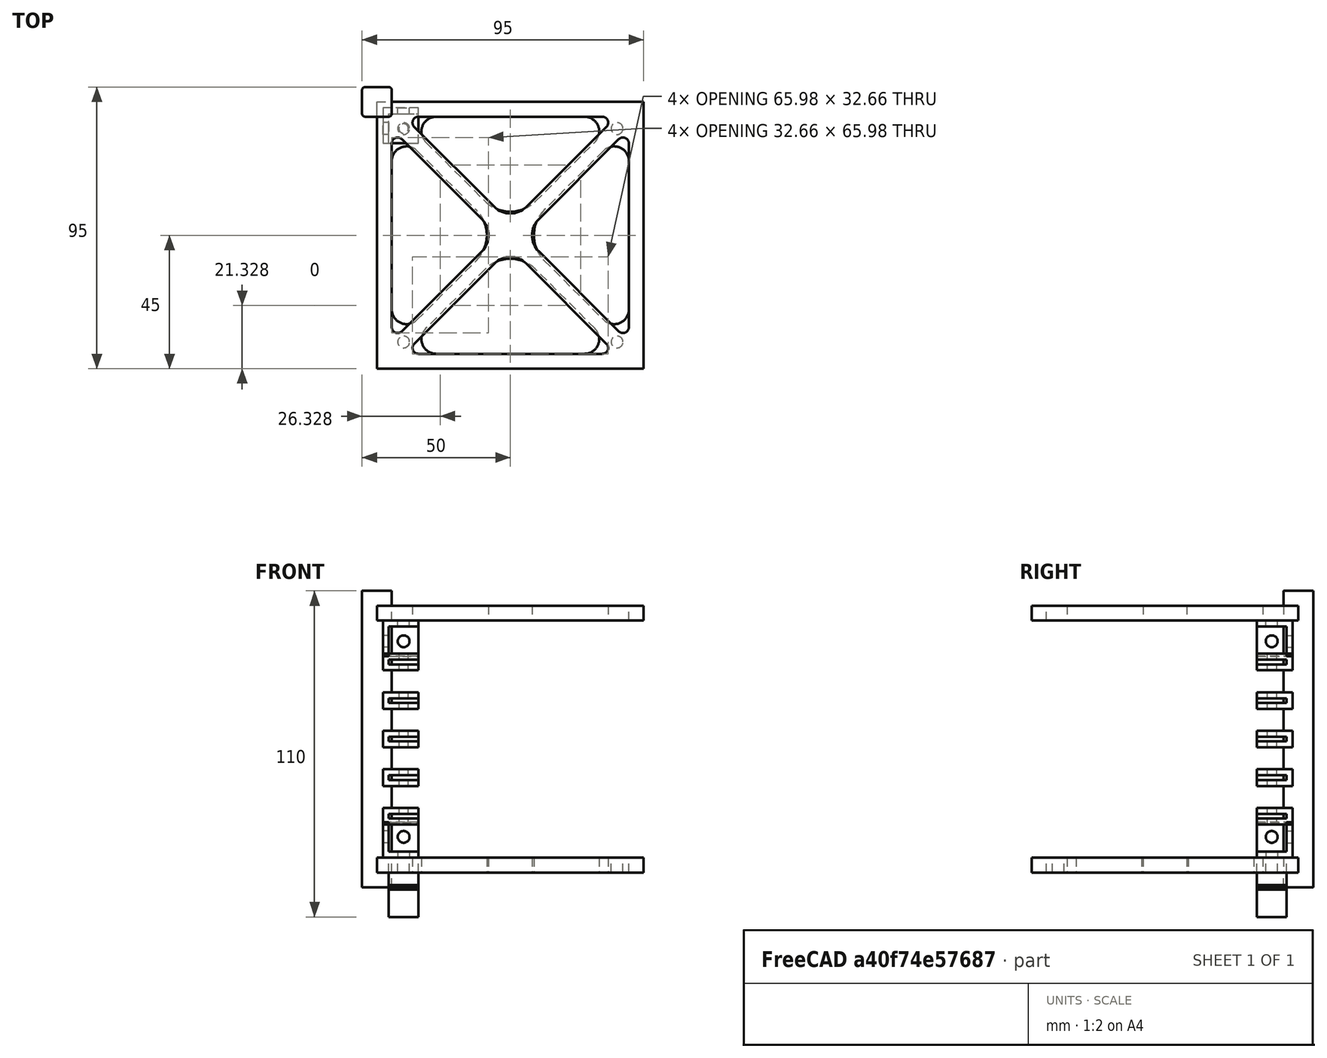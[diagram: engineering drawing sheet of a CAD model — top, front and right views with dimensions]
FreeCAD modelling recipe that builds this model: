
FCSTD DOCUMENT  (FreeCAD 0.19R24366 (Git))
Label: cube
License: Public Domain
LicenseURL: http://en.wikipedia.org/wiki/Public_domain
objects: Sketcher::SketchObject×25, PartDesign::Pad×18, PartDesign::Body×18, PartDesign::Boolean×10, PartDesign::Hole×7, App::Link×6, PartDesign::CoordinateSystem×3, App::DocumentObjectGroup×3, App::Part×3, PartDesign::Mirrored×2, PartDesign::MultiTransform×1, App::FeaturePython×1, Fem::FemSolverObjectPython×1, Fem::FemMeshShapeNetgenObject×1, Fem::ConstraintFixed×1, Fem::ConstraintForce×1, App::MaterialObjectPython×1, Fem::FemAnalysis×1
note: 109 computed .brp shape members not serialized (recipe doc carries the construction recipe); baked Part::Feature solids carry a one-line shape summary decoded from their .brp

FEATURE [Sketcher::SketchObject] Sketch
  FullyConstrained = true
  MapMode = 5
  Support = -> [XY_Plane001]
  sketch-geometry (28):
    g0: LineSegment StartX=-45 StartY=45 StartZ=0 EndX=45 EndY=45 EndZ=0
    g1: LineSegment StartX=45 StartY=45 StartZ=0 EndX=45 EndY=-45 EndZ=0
    g2: LineSegment StartX=45 StartY=-45 StartZ=0 EndX=-45 EndY=-45 EndZ=0
    g3: LineSegment StartX=-45 StartY=-45 StartZ=0 EndX=-45 EndY=45 EndZ=0
    g4: LineSegment StartX=-31 StartY=40 StartZ=0 EndX=31 EndY=40 EndZ=0
    g5: LineSegment StartX=-31 StartY=-40 StartZ=0 EndX=31 EndY=-40 EndZ=0
    g6: LineSegment StartX=-40 StartY=31 StartZ=0 EndX=-40 EndY=-31 EndZ=0
    g7: LineSegment StartX=40 StartY=31 StartZ=0 EndX=40 EndY=-31 EndZ=0
    g8: LineSegment StartX=-36.5858 StartY=32.4142 StartZ=0 EndX=-9.58579 EndY=5.41421 EndZ=0
    g9: LineSegment StartX=-32.4142 StartY=36.5858 StartZ=0 EndX=-5.41421 EndY=9.58579 EndZ=0
    g10: LineSegment StartX=5.41421 StartY=9.58579 StartZ=0 EndX=32.4142 EndY=36.5858 EndZ=0
    g11: LineSegment StartX=36.5858 StartY=32.4142 StartZ=0 EndX=9.58579 EndY=5.41421 EndZ=0
    g12: LineSegment StartX=9.58579 StartY=-5.41421 StartZ=0 EndX=36.5858 EndY=-32.4142 EndZ=0
    g13: LineSegment StartX=32.4142 StartY=-36.5858 StartZ=0 EndX=5.41421 EndY=-9.58579 EndZ=0
    g14: LineSegment StartX=-5.41421 StartY=-9.58579 StartZ=0 EndX=-32.4142 EndY=-36.5858 EndZ=0
    g15: LineSegment StartX=-36.5858 StartY=-32.4142 StartZ=0 EndX=-9.58579 EndY=-5.41421 EndZ=0
    g16: ArcOfCircle CenterX=38 CenterY=31 CenterZ=0 NormalX=0 NormalY=0 NormalZ=1 AngleXU=0 Radius=2 StartAngle=0 EndAngle=2.35619
    g17: ArcOfCircle CenterX=38 CenterY=-31 CenterZ=0 NormalX=0 NormalY=0 NormalZ=1 AngleXU=0 Radius=2 StartAngle=3.92699 EndAngle=6.28319
    g18: ArcOfCircle CenterX=31 CenterY=-38 CenterZ=0 NormalX=0 NormalY=0 NormalZ=1 AngleXU=0 Radius=2 StartAngle=4.71239 EndAngle=7.06858
    g19: ArcOfCircle CenterX=-31 CenterY=-38 CenterZ=0 NormalX=0 NormalY=0 NormalZ=1 AngleXU=0 Radius=2 StartAngle=2.35619 EndAngle=4.71239
    g20: ArcOfCircle CenterX=-38 CenterY=-31 CenterZ=0 NormalX=0 NormalY=0 NormalZ=1 AngleXU=0 Radius=2 StartAngle=3.14159 EndAngle=5.49779
    g21: ArcOfCircle CenterX=-38 CenterY=31 CenterZ=0 NormalX=0 NormalY=0 NormalZ=1 AngleXU=0 Radius=2 StartAngle=0.785398 EndAngle=3.14159
    g22: ArcOfCircle CenterX=-31 CenterY=38 CenterZ=0 NormalX=0 NormalY=0 NormalZ=1 AngleXU=0 Radius=2 StartAngle=1.5708 EndAngle=3.92699
    g23: ArcOfCircle CenterX=31 CenterY=38 CenterZ=0 NormalX=0 NormalY=0 NormalZ=1 AngleXU=0 Radius=2 StartAngle=5.49779 EndAngle=7.85398
    g24: ArcOfCircle CenterX=-15 CenterY=0 CenterZ=0 NormalX=0 NormalY=0 NormalZ=1 AngleXU=0 Radius=7.65685 StartAngle=5.49779 EndAngle=7.06858
    g25: ArcOfCircle CenterX=0 CenterY=15 CenterZ=0 NormalX=0 NormalY=0 NormalZ=1 AngleXU=0 Radius=7.65685 StartAngle=3.92699 EndAngle=5.49779
    g26: ArcOfCircle CenterX=15 CenterY=0 CenterZ=0 NormalX=0 NormalY=0 NormalZ=1 AngleXU=0 Radius=7.65685 StartAngle=2.35619 EndAngle=3.92699
    g27: ArcOfCircle CenterX=-6e-16 CenterY=-15 CenterZ=0 NormalX=0 NormalY=0 NormalZ=1 AngleXU=0 Radius=7.65685 StartAngle=0.785398 EndAngle=2.35619
  constraints (67):
    c: Coincident(g0,g1)
    c: Coincident(g1,g2)
    c: Coincident(g2,g3)
    c: Coincident(g3,g0)
    c: Horizontal(g0)
    c: Horizontal(g2)
    c: Vertical(g1)
    c: Vertical(g3)
    c: Symmetric(g0,g1,g-1)
    c: Equal(g2,g1)
    c: Horizontal(g4)
    c: Horizontal(g5)
    c: Vertical(g6)
    c: Vertical(g7)
    c: DistanceY(g3,g3) = 90
    c: Parallel(g8,g9)
    c: Parallel(g9,g12)
    c: Parallel(g12,g13)
    c: Parallel(g15,g14)
    c: Parallel(g14,g10)
    c: Parallel(g10,g11)
    c: Tangent(g11,g16) = -1.5708
    c: Tangent(g7,g16) = 1.5708
    c: Tangent(g12,g17) = -1.5708
    c: Tangent(g7,g17) = 1.5708
    c: Tangent(g13,g18) = -1.5708
    c: Tangent(g5,g18) = -1.5708
    c: Tangent(g14,g19) = -1.5708
    c: Tangent(g5,g19) = -1.5708
    c: Tangent(g15,g20) = -1.5708
    c: Tangent(g6,g20) = -1.5708
    c: Tangent(g6,g21) = -1.5708
    c: Tangent(g8,g21) = 1.5708
    c: Tangent(g9,g22) = -1.5708
    c: Tangent(g4,g22) = 1.5708
    c: Tangent(g4,g23) = 1.5708
    c: Tangent(g10,g23) = -1.5708
    c: Tangent(g8,g24) = 1.5708
    c: Tangent(g15,g24) = -1.5708
    c: Tangent(g9,g25) = -1.5708
    c: Tangent(g10,g25) = -1.5708
    c: Tangent(g11,g26) = -1.5708
    c: Tangent(g12,g26) = -1.5708
    c: Tangent(g13,g27) = -1.5708
    c: Tangent(g14,g27) = -1.5708
    c: Symmetric(g8,g12,g-1)
    c: PointOnObject(g24,g-1)
    c: PointOnObject(g26,g-1)
    c: Symmetric(g10,g14,g-1)
    c: Symmetric(g21,g17,g-1)
    c: Symmetric(g19,g23,g-1)
    c: Vertical(g21,g20)
    c: Horizontal(g18,g19)
    c: Vertical(g15,g8)
    c: Equal(g25,g24)
    c: Equal(g26,g27)
    c: PointOnObject(g25,g-2)
    c: Horizontal(g16,g21)
    c: Equal(g4,g5)
    c: Equal(g6,g5)
    c: DistanceX(g2,g6) = 5
    c: DistanceY(g2,g5) = 5
    c: DistanceX(g18,g1) = 14
    c: DistanceX(g26,g1) = 30
    c: DistanceY(g1,g18) = 7
    c: Perpendicular(g11,g8)
    c: DistanceX(g17,g1) = 7
FEATURE [PartDesign::Pad] Pad
  Direction = (1,1,1)
  Length = 5
  Length2 = 100
  Profile = -> Sketch
  Refine = true
  Type = 0
FEATURE [PartDesign::Body] Body  label="BottomCutout"
  Group = -> [Sketch,Pad]
  Origin = -> Origin001
  Placement = pos=(0,0,5) rot=(0,0,1;0rad)
  Tip = -> Pad
FEATURE [Sketcher::SketchObject] Sketch001
  FullyConstrained = true
  MapMode = 5
  Support = -> [XY_Plane003]
  sketch-geometry (8):
    g0: LineSegment StartX=-49 StartY=50 StartZ=0 EndX=-41 EndY=50 EndZ=0
    g1: LineSegment StartX=-40 StartY=49 StartZ=0 EndX=-40 EndY=41 EndZ=0
    g2: LineSegment StartX=-41 StartY=40 StartZ=0 EndX=-49 EndY=40 EndZ=0
    g3: LineSegment StartX=-50 StartY=41 StartZ=0 EndX=-50 EndY=49 EndZ=0
    g4: ArcOfCircle CenterX=-49 CenterY=41 CenterZ=0 NormalX=0 NormalY=0 NormalZ=1 AngleXU=0 Radius=1 StartAngle=3.14159 EndAngle=4.71239
    g5: ArcOfCircle CenterX=-41 CenterY=41 CenterZ=0 NormalX=0 NormalY=0 NormalZ=1 AngleXU=0 Radius=1 StartAngle=4.71239 EndAngle=6.28319
    g6: ArcOfCircle CenterX=-41 CenterY=49 CenterZ=0 NormalX=0 NormalY=0 NormalZ=1 AngleXU=0 Radius=1 StartAngle=7.1e-14 EndAngle=1.5708
    g7: ArcOfCircle CenterX=-49 CenterY=49 CenterZ=0 NormalX=0 NormalY=0 NormalZ=1 AngleXU=0 Radius=1 StartAngle=1.5708 EndAngle=3.14159
  constraints (20):
    c: Horizontal(g0)
    c: Horizontal(g2)
    c: Vertical(g1)
    c: Vertical(g3)
    c: Equal(g3,g2)
    c: Tangent(g3,g4) = 1.5708
    c: Tangent(g2,g4) = 1.5708
    c: Tangent(g2,g5) = 1.5708
    c: Tangent(g1,g5) = 1.5708
    c: Tangent(g1,g6) = 1.5708
    c: Tangent(g0,g6) = 1.5708
    c: Tangent(g3,g7) = 1.5708
    c: Tangent(g0,g7) = 1.5708
    c: Equal(g7,g6)
    c: Equal(g6,g5)
    c: Equal(g5,g4)
    c: DistanceY(g2,g0) = 10
    c: Radius(g4) = 1
    c: DistanceY(g-1,g2) = 40
    c: DistanceX(g1,g-1) = 40
FEATURE [PartDesign::Pad] Pad001  label="padHeight"
  Direction = (1,1,1)
  Length = 100
  Length2 = 100
  Profile = -> Sketch001
  Refine = true
  Type = 0
FEATURE [Sketcher::SketchObject] Sketch002
  FullyConstrained = true
  MapMode = 5
  Support = -> [XY_Plane005]
  sketch-geometry (4):
    g0: LineSegment StartX=-41 StartY=41 StartZ=0 EndX=-31 EndY=41 EndZ=0
    g1: LineSegment StartX=-31 StartY=41 StartZ=0 EndX=-31 EndY=31 EndZ=0
    g2: LineSegment StartX=-31 StartY=31 StartZ=0 EndX=-41 EndY=31 EndZ=0
    g3: LineSegment StartX=-41 StartY=31 StartZ=0 EndX=-41 EndY=41 EndZ=0
  constraints (12):
    c: Coincident(g0,g1)
    c: Coincident(g1,g2)
    c: Coincident(g2,g3)
    c: Coincident(g3,g0)
    c: Horizontal(g0)
    c: Horizontal(g2)
    c: Vertical(g1)
    c: Vertical(g3)
    c: Equal(g3,g2)
    c: Distance(g1) = 10
    c: DistanceX(g-1,g2) = -41
    c: DistanceY(g-1,g2) = 31
FEATURE [Sketcher::SketchObject] Sketch003
  FullyConstrained = true
  MapMode = 5
  Support = -> [XY_Plane004]
  sketch-geometry (4):
    g0: LineSegment StartX=-43 StartY=31 StartZ=0 EndX=-31 EndY=31 EndZ=0
    g1: LineSegment StartX=-31 StartY=31 StartZ=0 EndX=-31 EndY=43 EndZ=0
    g2: LineSegment StartX=-31 StartY=43 StartZ=0 EndX=-43 EndY=43 EndZ=0
    g3: LineSegment StartX=-43 StartY=43 StartZ=0 EndX=-43 EndY=31 EndZ=0
  constraints (12):
    c: Coincident(g1,g2)
    c: Coincident(g2,g3)
    c: Coincident(g3,g0)
    c: Horizontal(g0)
    c: Horizontal(g2)
    c: Vertical(g1)
    c: Vertical(g3)
    c: Equal(g3,g0)
    c: Coincident(g0,g1)
    c: Distance(g1,g0) = 12
    c: DistanceY(g-1,g0) = 31
    c: DistanceX(g0,g-1) = 31
FEATURE [PartDesign::Pad] Pad002
  Direction = (1,1,1)
  Length = 12
  Length2 = 100
  Profile = -> Sketch003
  Refine = true
  Reversed = true
  Type = 0
FEATURE [PartDesign::Pad] Pad003
  Direction = (1,1,1)
  Length = 10
  Length2 = 100
  Profile = -> Sketch002
  Refine = true
  Reversed = true
  Type = 0
FEATURE [PartDesign::Body] Body003  label="Neg_Corner"
  Group = -> [Sketch002,Pad003]
  Origin = -> Origin005
  Tip = -> Pad003
FEATURE [PartDesign::Boolean] Boolean001
  BaseFeature = -> Pad002
  Group = -> [Body003]
  Refine = true
  Type = 1
FEATURE [Sketcher::SketchObject] Sketch004
  FullyConstrained = true
  MapMode = 5
  Support = -> [XY_Plane006]
  sketch-geometry (28):
    g0: LineSegment StartX=-45 StartY=45 StartZ=0 EndX=45 EndY=45 EndZ=0
    g1: LineSegment StartX=45 StartY=45 StartZ=0 EndX=45 EndY=-45 EndZ=0
    g2: LineSegment StartX=45 StartY=-45 StartZ=0 EndX=-45 EndY=-45 EndZ=0
    g3: LineSegment StartX=-45 StartY=-45 StartZ=0 EndX=-45 EndY=45 EndZ=0
    g4: LineSegment StartX=-25 StartY=40 StartZ=0 EndX=25 EndY=40 EndZ=0
    g5: LineSegment StartX=-25 StartY=-40 StartZ=0 EndX=25 EndY=-40 EndZ=0
    g6: LineSegment StartX=-40 StartY=25 StartZ=0 EndX=-40 EndY=-25 EndZ=0
    g7: LineSegment StartX=40 StartY=25 StartZ=0 EndX=40 EndY=-25 EndZ=0
    g8: LineSegment StartX=-31.4645 StartY=28.5355 StartZ=0 EndX=-11.4645 EndY=8.53553 EndZ=0
    g9: LineSegment StartX=-28.5355 StartY=31.4645 StartZ=0 EndX=-8.53553 EndY=11.4645 EndZ=0
    g10: LineSegment StartX=8.53553 StartY=11.4645 StartZ=0 EndX=28.5355 EndY=31.4645 EndZ=0
    g11: LineSegment StartX=31.4645 StartY=28.5355 StartZ=0 EndX=11.4645 EndY=8.53553 EndZ=0
    g12: LineSegment StartX=11.4645 StartY=-8.53553 StartZ=0 EndX=31.4645 EndY=-28.5355 EndZ=0
    g13: LineSegment StartX=28.5355 StartY=-31.4645 StartZ=0 EndX=8.53553 EndY=-11.4645 EndZ=0
    g14: LineSegment StartX=-8.53553 StartY=-11.4645 StartZ=0 EndX=-28.5355 EndY=-31.4645 EndZ=0
    g15: LineSegment StartX=-31.4645 StartY=-28.5355 StartZ=0 EndX=-11.4645 EndY=-8.53553 EndZ=0
    g16: ArcOfCircle CenterX=35 CenterY=25 CenterZ=0 NormalX=0 NormalY=0 NormalZ=1 AngleXU=0 Radius=5 StartAngle=0 EndAngle=2.35619
    g17: ArcOfCircle CenterX=35 CenterY=-25 CenterZ=0 NormalX=0 NormalY=0 NormalZ=1 AngleXU=0 Radius=5 StartAngle=3.92699 EndAngle=6.28319
    g18: ArcOfCircle CenterX=25 CenterY=-35 CenterZ=0 NormalX=0 NormalY=0 NormalZ=1 AngleXU=0 Radius=5 StartAngle=4.71239 EndAngle=7.06858
    g19: ArcOfCircle CenterX=-25 CenterY=-35 CenterZ=0 NormalX=0 NormalY=0 NormalZ=1 AngleXU=0 Radius=5 StartAngle=2.35619 EndAngle=4.71239
    g20: ArcOfCircle CenterX=-35 CenterY=-25 CenterZ=0 NormalX=0 NormalY=0 NormalZ=1 AngleXU=0 Radius=5 StartAngle=3.14159 EndAngle=5.49779
    g21: ArcOfCircle CenterX=-35 CenterY=25 CenterZ=0 NormalX=0 NormalY=0 NormalZ=1 AngleXU=0 Radius=5 StartAngle=0.785398 EndAngle=3.14159
    g22: ArcOfCircle CenterX=-25 CenterY=35 CenterZ=0 NormalX=0 NormalY=0 NormalZ=1 AngleXU=0 Radius=5 StartAngle=1.5708 EndAngle=3.92699
    g23: ArcOfCircle CenterX=25 CenterY=35 CenterZ=0 NormalX=0 NormalY=0 NormalZ=1 AngleXU=0 Radius=5 StartAngle=5.49779 EndAngle=7.85398
    g24: ArcOfCircle CenterX=-20 CenterY=0 CenterZ=0 NormalX=0 NormalY=0 NormalZ=1 AngleXU=0 Radius=12.0711 StartAngle=5.49779 EndAngle=7.06858
    g25: ArcOfCircle CenterX=0 CenterY=20 CenterZ=0 NormalX=0 NormalY=0 NormalZ=1 AngleXU=0 Radius=12.0711 StartAngle=3.92699 EndAngle=5.49779
    g26: ArcOfCircle CenterX=20 CenterY=0 CenterZ=0 NormalX=0 NormalY=0 NormalZ=1 AngleXU=0 Radius=12.0711 StartAngle=2.35619 EndAngle=3.92699
    g27: ArcOfCircle CenterX=1.6498e-12 CenterY=-20 CenterZ=0 NormalX=0 NormalY=0 NormalZ=1 AngleXU=0 Radius=12.0711 StartAngle=0.785398 EndAngle=2.35619
  constraints (67):
    c: Coincident(g0,g1)
    c: Coincident(g1,g2)
    c: Coincident(g2,g3)
    c: Coincident(g3,g0)
    c: Horizontal(g0)
    c: Horizontal(g2)
    c: Vertical(g1)
    c: Vertical(g3)
    c: Symmetric(g0,g1,g-1)
    c: Equal(g2,g1)
    c: Horizontal(g4)
    c: Horizontal(g5)
    c: Vertical(g6)
    c: Vertical(g7)
    c: DistanceY(g3,g3) = 90
    c: Parallel(g8,g9)
    c: Parallel(g9,g12)
    c: Parallel(g12,g13)
    c: Parallel(g15,g14)
    c: Parallel(g14,g10)
    c: Parallel(g10,g11)
    c: Tangent(g11,g16) = -1.5708
    c: Tangent(g7,g16) = 1.5708
    c: Tangent(g12,g17) = -1.5708
    c: Tangent(g7,g17) = 1.5708
    c: Tangent(g13,g18) = -1.5708
    c: Tangent(g5,g18) = -1.5708
    c: Tangent(g14,g19) = -1.5708
    c: Tangent(g5,g19) = -1.5708
    c: Tangent(g15,g20) = -1.5708
    c: Tangent(g6,g20) = -1.5708
    c: Tangent(g6,g21) = -1.5708
    c: Tangent(g8,g21) = 1.5708
    c: Tangent(g9,g22) = -1.5708
    c: Tangent(g4,g22) = 1.5708
    c: Tangent(g4,g23) = 1.5708
    c: Tangent(g10,g23) = -1.5708
    c: Tangent(g8,g24) = 1.5708
    c: Tangent(g15,g24) = -1.5708
    c: Tangent(g9,g25) = -1.5708
    c: Tangent(g10,g25) = -1.5708
    c: Tangent(g11,g26) = -1.5708
    c: Tangent(g12,g26) = -1.5708
    c: Tangent(g13,g27) = -1.5708
    c: Tangent(g14,g27) = -1.5708
    c: Symmetric(g8,g12,g-1)
    c: PointOnObject(g24,g-1)
    c: PointOnObject(g26,g-1)
    c: Symmetric(g10,g14,g-1)
    c: Symmetric(g21,g17,g-1)
    c: Symmetric(g19,g23,g-1)
    c: Vertical(g21,g20)
    c: Horizontal(g18,g19)
    c: Vertical(g15,g8)
    c: Equal(g25,g24)
    c: Equal(g26,g27)
    c: PointOnObject(g25,g-2)
    c: Horizontal(g16,g21)
    c: Equal(g4,g5)
    c: Equal(g6,g5)
    c: DistanceX(g2,g6) = 5
    c: DistanceY(g2,g5) = 5
    c: DistanceX(g18,g1) = 20
    c: DistanceX(g26,g1) = 25
    c: DistanceY(g1,g18) = 10
    c: Perpendicular(g11,g8)
    c: DistanceX(g17,g1) = 10
FEATURE [PartDesign::Pad] Pad004
  Direction = (1,1,1)
  Length = 5
  Length2 = 100
  Profile = -> Sketch004
  Refine = true
  Type = 0
FEATURE [Sketcher::SketchObject] Sketch005  label="yCornerHoleSketch"
  FullyConstrained = true
  MapMode = 5
  Placement = pos=(0,0,0) rot=(1,0,0;1.5708rad)
  Support = -> [XZ_Plane004]
  sketch-geometry (1):
    g0: Circle CenterX=-36 CenterY=-5 CenterZ=0 NormalX=0 NormalY=0 NormalZ=1 AngleXU=0 Radius=2
  constraints (3):
    c: DistanceY(g0,g-1) = 5
    c: DistanceX(g-1,g0) = -36
    c: Radius(g0) = 2
FEATURE [PartDesign::Hole] Hole  label="yCornerHole"
  BaseFeature = -> Boolean001
  Depth = 25
  DepthType = 1
  Diameter = 4
  DrillForDepth = false
  DrillPoint = 1
  DrillPointAngle = 118
  HoleCutCountersinkAngle = 90
  HoleCutCustomValues = false
  HoleCutDepth = 0
  HoleCutDiameter = 4.1
  HoleCutType = 2
  ModelActualThread = false
  Profile = -> Sketch005
  Refine = true
  Tapered = false
  TaperedAngle = 90
  ThreadAngle = 0
  ThreadClass = 0
  ThreadCutOffInner = 0
  ThreadCutOffOuter = 0
  ThreadDirection = 0
  ThreadFit = 0
  ThreadPitch = 0
  ThreadSize = 0
  ThreadType = 0
  Threaded = false
FEATURE [Sketcher::SketchObject] Sketch006  label="zConerHoleSketch"
  FullyConstrained = true
  MapMode = 5
  Placement = pos=(0,0,-10) rot=(0,0,1;0rad)
  Support = -> [Hole]
  sketch-geometry (1):
    g0: Circle CenterX=-36 CenterY=36 CenterZ=0 NormalX=0 NormalY=0 NormalZ=1 AngleXU=0 Radius=2
  constraints (3):
    c: DistanceX(g-1,g0) = -36
    c: DistanceY(g-1,g0) = 36
    c: Radius(g0) = 2
FEATURE [PartDesign::Hole] Hole001  label="zCornerHole"
  BaseFeature = -> Hole
  Depth = 25
  DepthType = 0
  Diameter = 4
  DrillForDepth = false
  DrillPoint = 1
  DrillPointAngle = 118
  HoleCutCountersinkAngle = 90
  HoleCutCustomValues = false
  HoleCutDepth = 0
  HoleCutDiameter = 6.1
  HoleCutType = 0
  ModelActualThread = false
  Profile = -> Sketch006
  Refine = true
  Tapered = false
  TaperedAngle = 90
  ThreadAngle = 0
  ThreadClass = 0
  ThreadCutOffInner = 0
  ThreadCutOffOuter = 0
  ThreadDirection = 0
  ThreadFit = 0
  ThreadPitch = 0
  ThreadSize = 0
  ThreadType = 0
  Threaded = false
FEATURE [Sketcher::SketchObject] Sketch007  label="xCornerHoleSketch"
  FullyConstrained = true
  MapMode = 5
  Placement = pos=(-41,0,0) rot=(0.57735,0.57735,0.57735;2.0944rad)
  Support = -> [Hole001]
  sketch-geometry (1):
    g0: Circle CenterX=36 CenterY=-5 CenterZ=0 NormalX=0 NormalY=0 NormalZ=1 AngleXU=0 Radius=2
  constraints (3):
    c: DistanceY(g0,g-1) = 5
    c: DistanceX(g-1,g0) = 36
    c: Radius(g0) = 2
FEATURE [PartDesign::Hole] Hole002  label="xCornerHole"
  BaseFeature = -> Hole001
  Depth = 25
  DepthType = 0
  Diameter = 4
  DrillForDepth = false
  DrillPoint = 1
  DrillPointAngle = 118
  HoleCutCountersinkAngle = 90
  HoleCutCustomValues = false
  HoleCutDepth = 0
  HoleCutDiameter = 6.1
  HoleCutType = 0
  ModelActualThread = false
  Profile = -> Sketch007
  Refine = true
  Tapered = false
  TaperedAngle = 90
  ThreadAngle = 0
  ThreadClass = 0
  ThreadCutOffInner = 0
  ThreadCutOffOuter = 0
  ThreadDirection = 0
  ThreadFit = 0
  ThreadPitch = 0
  ThreadSize = 0
  ThreadType = 0
  Threaded = false
FEATURE [PartDesign::Body] Body002  label="BottomCorner"
  Group = -> [Sketch003,Pad002,Boolean001,Sketch005,Hole,Sketch006,Hole001,Sketch007,Hole002]
  Origin = -> Origin004
  Placement = pos=(0,0,22) rot=(0,0,1;0rad)
  Tip = -> Hole002
FEATURE [Sketcher::SketchObject] Sketch009  label="topLeftHoleSketch"
  FullyConstrained = true
  MapMode = 5
  Placement = pos=(0,0,-10) rot=(0,0,1;0rad)
  Support = -> [Hole]
  sketch-geometry (1):
    g0: Circle CenterX=-36 CenterY=36 CenterZ=0 NormalX=0 NormalY=0 NormalZ=1 AngleXU=0 Radius=2
  constraints (3):
    c: DistanceX(g-1,g0) = -36
    c: DistanceY(g-1,g0) = 36
    c: Radius(g0) = 2
FEATURE [PartDesign::Hole] Hole004  label="topLeftHole"
  BaseFeature = -> Pad004
  Depth = 25
  DepthType = 1
  Diameter = 4
  DrillForDepth = false
  DrillPoint = 1
  DrillPointAngle = 118
  HoleCutCountersinkAngle = 90
  HoleCutCustomValues = false
  HoleCutDepth = 0
  HoleCutDiameter = 6.1
  HoleCutType = 0
  ModelActualThread = false
  Profile = -> Sketch009
  Refine = true
  Reversed = true
  Tapered = false
  TaperedAngle = 90
  ThreadAngle = 0
  ThreadClass = 0
  ThreadCutOffInner = 0
  ThreadCutOffOuter = 0
  ThreadDirection = 0
  ThreadFit = 0
  ThreadPitch = 0
  ThreadSize = 0
  ThreadType = 0
  Threaded = false
FEATURE [PartDesign::Mirrored] Mirrored001
  MirrorPlane = -> Sketch009 [V_Axis]
  Refine = true
FEATURE [PartDesign::Mirrored] Mirrored002
  MirrorPlane = -> Sketch009 [H_Axis]
  Refine = true
FEATURE [PartDesign::MultiTransform] MultiTransform001
  BaseFeature = -> Hole004
  Originals = -> [Hole004]
  Refine = true
  Transformations = -> [Mirrored001,Mirrored002]
FEATURE [PartDesign::Body] Body004  label="Plate001"
  Group = -> [Sketch004,Pad004,Sketch009,Hole004,MultiTransform001,Mirrored001,Mirrored002]
  Origin = -> Origin006
  Placement = pos=(0,0,5) rot=(0,0,1;0rad)
  Tip = -> MultiTransform001
FEATURE [PartDesign::CoordinateSystem] LCS_Origin
  AttacherType = Attacher::AttachEngine3D
  MapMode = 2
  Support = -> [X_Axis007]
FEATURE [App::FeaturePython] Variables  # WARN: FeaturePython — macro-defined, semantics opaque (R4)
  Type = App::PropertyContainer
FEATURE [App::DocumentObjectGroup] Constraints
FEATURE [App::DocumentObjectGroup] Configurations
FEATURE [App::Link] Bottom  label="Bottom001"
  LinkedObject = -> Part
FEATURE [PartDesign::CoordinateSystem] LCS_Plate
  AttacherType = Attacher::AttachEngine3D
  Support = -> [MultiTransform001]
FEATURE [App::Part] Part  label="Bottom"
  Group = -> [Body004,LCS_Plate]
  Origin = -> Origin
FEATURE [App::Link] Side  label="Side001"
  AttachedBy = #LCS_Side
  AttachedTo = Parent Assembly#LCS_Origin
  LinkedObject = -> Part001
  SolverId = Placement::ExpressionEngine
  expr: Placement = LCS_Origin.Placement * AttachmentOffset * LCS_Side.Placement ^ -1
FEATURE [App::Link] Side001  label="Side002"
  AttachedBy = #LCS_Side
  AttachedTo = Bottom#LCS_Plate
  AttachmentOffset = pos=(0,0,0) rot=(0,0,1;1.5708rad)
  LinkPlacement = pos=(0,0,0) rot=(0,0,1;1.5708rad)
  LinkedObject = -> Part001
  Placement = pos=(0,0,0) rot=(0,0,1;1.5708rad)
  SolverId = Placement::ExpressionEngine
  expr: Placement = Bottom.Placement * LCS_Plate.Placement * AttachmentOffset * LCS_Side.Placement ^ -1
FEATURE [App::Link] Side002  label="Side003"
  AttachedBy = #LCS_Side
  AttachedTo = Bottom#LCS_Plate
  AttachmentOffset = pos=(0,0,0) rot=(0,0,1;3.14159rad)
  LinkPlacement = pos=(0,0,0) rot=(0,0,1;3.14159rad)
  LinkedObject = -> Part001
  Placement = pos=(0,0,0) rot=(0,0,1;3.14159rad)
  SolverId = Placement::ExpressionEngine
  expr: Placement = Bottom.Placement * LCS_Plate.Placement * AttachmentOffset * LCS_Side.Placement ^ -1
FEATURE [App::Link] Side003  label="Side004"
  AttachedBy = #LCS_Side
  AttachedTo = Bottom#LCS_Plate
  AttachmentOffset = pos=(0,0,0) rot=(0,0,1;4.71239rad)
  LinkPlacement = pos=(0,0,0) rot=(0,0,1;4.71239rad)
  LinkedObject = -> Part001
  Placement = pos=(0,0,0) rot=(0,0,1;4.71239rad)
  SolverId = Placement::ExpressionEngine
  expr: Placement = Bottom.Placement * LCS_Plate.Placement * AttachmentOffset * LCS_Side.Placement ^ -1
FEATURE [Sketcher::SketchObject] Sketch010
  FullyConstrained = true
  MapMode = 5
  Support = -> [XY_Plane008]
  sketch-geometry (28):
    g0: LineSegment StartX=-45 StartY=45 StartZ=0 EndX=45 EndY=45 EndZ=0
    g1: LineSegment StartX=45 StartY=45 StartZ=0 EndX=45 EndY=-45 EndZ=0
    g2: LineSegment StartX=45 StartY=-45 StartZ=0 EndX=-45 EndY=-45 EndZ=0
    g3: LineSegment StartX=-45 StartY=-45 StartZ=0 EndX=-45 EndY=45 EndZ=0
    g4: LineSegment StartX=-31 StartY=40 StartZ=0 EndX=31 EndY=40 EndZ=0
    g5: LineSegment StartX=-31 StartY=-40 StartZ=0 EndX=31 EndY=-40 EndZ=0
    g6: LineSegment StartX=-40 StartY=31 StartZ=0 EndX=-40 EndY=-31 EndZ=0
    g7: LineSegment StartX=40 StartY=31 StartZ=0 EndX=40 EndY=-31 EndZ=0
    g8: LineSegment StartX=-36.5858 StartY=32.4142 StartZ=0 EndX=-9.58579 EndY=5.41421 EndZ=0
    g9: LineSegment StartX=-32.4142 StartY=36.5858 StartZ=0 EndX=-5.41421 EndY=9.58579 EndZ=0
    g10: LineSegment StartX=5.41421 StartY=9.58579 StartZ=0 EndX=32.4142 EndY=36.5858 EndZ=0
    g11: LineSegment StartX=36.5858 StartY=32.4142 StartZ=0 EndX=9.58579 EndY=5.41421 EndZ=0
    g12: LineSegment StartX=9.58579 StartY=-5.41421 StartZ=0 EndX=36.5858 EndY=-32.4142 EndZ=0
    g13: LineSegment StartX=32.4142 StartY=-36.5858 StartZ=0 EndX=5.41421 EndY=-9.58579 EndZ=0
    g14: LineSegment StartX=-5.41421 StartY=-9.58579 StartZ=0 EndX=-32.4142 EndY=-36.5858 EndZ=0
    g15: LineSegment StartX=-36.5858 StartY=-32.4142 StartZ=0 EndX=-9.58579 EndY=-5.41421 EndZ=0
    g16: ArcOfCircle CenterX=38 CenterY=31 CenterZ=0 NormalX=0 NormalY=0 NormalZ=1 AngleXU=0 Radius=2 StartAngle=0 EndAngle=2.35619
    g17: ArcOfCircle CenterX=38 CenterY=-31 CenterZ=0 NormalX=0 NormalY=0 NormalZ=1 AngleXU=0 Radius=2 StartAngle=3.92699 EndAngle=6.28319
    g18: ArcOfCircle CenterX=31 CenterY=-38 CenterZ=0 NormalX=0 NormalY=0 NormalZ=1 AngleXU=0 Radius=2 StartAngle=4.71239 EndAngle=7.06858
    g19: ArcOfCircle CenterX=-31 CenterY=-38 CenterZ=0 NormalX=0 NormalY=0 NormalZ=1 AngleXU=0 Radius=2 StartAngle=2.35619 EndAngle=4.71239
    g20: ArcOfCircle CenterX=-38 CenterY=-31 CenterZ=0 NormalX=0 NormalY=0 NormalZ=1 AngleXU=0 Radius=2 StartAngle=3.14159 EndAngle=5.49779
    g21: ArcOfCircle CenterX=-38 CenterY=31 CenterZ=0 NormalX=0 NormalY=0 NormalZ=1 AngleXU=0 Radius=2 StartAngle=0.785398 EndAngle=3.14159
    g22: ArcOfCircle CenterX=-31 CenterY=38 CenterZ=0 NormalX=0 NormalY=0 NormalZ=1 AngleXU=0 Radius=2 StartAngle=1.5708 EndAngle=3.92699
    g23: ArcOfCircle CenterX=31 CenterY=38 CenterZ=0 NormalX=0 NormalY=0 NormalZ=1 AngleXU=0 Radius=2 StartAngle=5.49779 EndAngle=7.85398
    g24: ArcOfCircle CenterX=-15 CenterY=0 CenterZ=0 NormalX=0 NormalY=0 NormalZ=1 AngleXU=0 Radius=7.65685 StartAngle=5.49779 EndAngle=7.06858
    g25: ArcOfCircle CenterX=0 CenterY=15 CenterZ=0 NormalX=0 NormalY=0 NormalZ=1 AngleXU=0 Radius=7.65685 StartAngle=3.92699 EndAngle=5.49779
    g26: ArcOfCircle CenterX=15 CenterY=0 CenterZ=0 NormalX=0 NormalY=0 NormalZ=1 AngleXU=0 Radius=7.65685 StartAngle=2.35619 EndAngle=3.92699
    g27: ArcOfCircle CenterX=-6e-16 CenterY=-15 CenterZ=0 NormalX=0 NormalY=0 NormalZ=1 AngleXU=0 Radius=7.65685 StartAngle=0.785398 EndAngle=2.35619
  constraints (67):
    c: Coincident(g0,g1)
    c: Coincident(g1,g2)
    c: Coincident(g2,g3)
    c: Coincident(g3,g0)
    c: Horizontal(g0)
    c: Horizontal(g2)
    c: Vertical(g1)
    c: Vertical(g3)
    c: Symmetric(g0,g1,g-1)
    c: Equal(g2,g1)
    c: Horizontal(g4)
    c: Horizontal(g5)
    c: Vertical(g6)
    c: Vertical(g7)
    c: DistanceY(g3,g3) = 90
    c: Parallel(g8,g9)
    c: Parallel(g9,g12)
    c: Parallel(g12,g13)
    c: Parallel(g15,g14)
    c: Parallel(g14,g10)
    c: Parallel(g10,g11)
    c: Tangent(g11,g16) = -1.5708
    c: Tangent(g7,g16) = 1.5708
    c: Tangent(g12,g17) = -1.5708
    c: Tangent(g7,g17) = 1.5708
    c: Tangent(g13,g18) = -1.5708
    c: Tangent(g5,g18) = -1.5708
    c: Tangent(g14,g19) = -1.5708
    c: Tangent(g5,g19) = -1.5708
    c: Tangent(g15,g20) = -1.5708
    c: Tangent(g6,g20) = -1.5708
    c: Tangent(g6,g21) = -1.5708
    c: Tangent(g8,g21) = 1.5708
    c: Tangent(g9,g22) = -1.5708
    c: Tangent(g4,g22) = 1.5708
    c: Tangent(g4,g23) = 1.5708
    c: Tangent(g10,g23) = -1.5708
    c: Tangent(g8,g24) = 1.5708
    c: Tangent(g15,g24) = -1.5708
    c: Tangent(g9,g25) = -1.5708
    c: Tangent(g10,g25) = -1.5708
    c: Tangent(g11,g26) = -1.5708
    c: Tangent(g12,g26) = -1.5708
    c: Tangent(g13,g27) = -1.5708
    c: Tangent(g14,g27) = -1.5708
    c: Symmetric(g8,g12,g-1)
    c: PointOnObject(g24,g-1)
    c: PointOnObject(g26,g-1)
    c: Symmetric(g10,g14,g-1)
    c: Symmetric(g21,g17,g-1)
    c: Symmetric(g19,g23,g-1)
    c: Vertical(g21,g20)
    c: Horizontal(g18,g19)
    c: Vertical(g15,g8)
    c: Equal(g25,g24)
    c: Equal(g26,g27)
    c: PointOnObject(g25,g-2)
    c: Horizontal(g16,g21)
    c: Equal(g4,g5)
    c: Equal(g6,g5)
    c: DistanceX(g2,g6) = 5
    c: DistanceY(g2,g5) = 5
    c: DistanceX(g18,g1) = 14
    c: DistanceX(g26,g1) = 30
    c: DistanceY(g1,g18) = 7
    c: Perpendicular(g11,g8)
    c: DistanceX(g17,g1) = 7
FEATURE [PartDesign::Pad] Pad005
  Direction = (1,1,1)
  Length = 5
  Length2 = 100
  Profile = -> Sketch010
  Refine = true
  Type = 0
FEATURE [PartDesign::Body] Body005  label="TopCutout"
  Group = -> [Sketch010,Pad005]
  Origin = -> Origin008
  Placement = pos=(0,0,90) rot=(0,0,1;0rad)
  Tip = -> Pad005
FEATURE [PartDesign::Boolean] Boolean  label="PlateCutouts"
  BaseFeature = -> Pad001
  Group = -> [Body,Body005]
  Refine = true
  Type = 1
FEATURE [Sketcher::SketchObject] Sketch011
  FullyConstrained = true
  MapMode = 5
  Support = -> [XY_Plane010]
  sketch-geometry (4):
    g0: LineSegment StartX=-41 StartY=41 StartZ=0 EndX=-31 EndY=41 EndZ=0
    g1: LineSegment StartX=-31 StartY=41 StartZ=0 EndX=-31 EndY=31 EndZ=0
    g2: LineSegment StartX=-31 StartY=31 StartZ=0 EndX=-41 EndY=31 EndZ=0
    g3: LineSegment StartX=-41 StartY=31 StartZ=0 EndX=-41 EndY=41 EndZ=0
  constraints (12):
    c: Coincident(g0,g1)
    c: Coincident(g1,g2)
    c: Coincident(g2,g3)
    c: Coincident(g3,g0)
    c: Horizontal(g0)
    c: Horizontal(g2)
    c: Vertical(g1)
    c: Vertical(g3)
    c: Equal(g3,g2)
    c: Distance(g1) = 10
    c: DistanceX(g-1,g2) = -41
    c: DistanceY(g-1,g2) = 31
FEATURE [Sketcher::SketchObject] Sketch012
  FullyConstrained = true
  MapMode = 5
  Support = -> [XY_Plane009]
  sketch-geometry (4):
    g0: LineSegment StartX=-43 StartY=31 StartZ=0 EndX=-31 EndY=31 EndZ=0
    g1: LineSegment StartX=-31 StartY=31 StartZ=0 EndX=-31 EndY=43 EndZ=0
    g2: LineSegment StartX=-31 StartY=43 StartZ=0 EndX=-43 EndY=43 EndZ=0
    g3: LineSegment StartX=-43 StartY=43 StartZ=0 EndX=-43 EndY=31 EndZ=0
  constraints (12):
    c: Coincident(g1,g2)
    c: Coincident(g2,g3)
    c: Coincident(g3,g0)
    c: Horizontal(g0)
    c: Horizontal(g2)
    c: Vertical(g1)
    c: Vertical(g3)
    c: Equal(g3,g0)
    c: Coincident(g0,g1)
    c: Distance(g1,g0) = 12
    c: DistanceY(g-1,g0) = 31
    c: DistanceX(g0,g-1) = 31
FEATURE [PartDesign::Pad] Pad006
  Direction = (1,1,1)
  Length = 12
  Length2 = 100
  Profile = -> Sketch012
  Refine = true
  Type = 0
FEATURE [PartDesign::Pad] Pad007
  Direction = (1,1,1)
  Length = 10
  Length2 = 100
  Profile = -> Sketch011
  Refine = true
  Type = 0
FEATURE [PartDesign::Body] Body007  label="Neg_Corner001"
  Group = -> [Sketch011,Pad007]
  Origin = -> Origin010
  Tip = -> Pad007
FEATURE [PartDesign::Boolean] Boolean003
  BaseFeature = -> Pad006
  Group = -> [Body007]
  Refine = true
  Type = 1
FEATURE [Sketcher::SketchObject] Sketch013  label="yCornerHoleSketch001"
  FullyConstrained = true
  MapMode = 5
  Placement = pos=(0,0,0) rot=(1,0,0;1.5708rad)
  Support = -> [XZ_Plane009]
  sketch-geometry (1):
    g0: Circle CenterX=-36 CenterY=5 CenterZ=0 NormalX=0 NormalY=0 NormalZ=1 AngleXU=0 Radius=2
  constraints (3):
    c: DistanceY(g0,g-1) = -5
    c: DistanceX(g-1,g0) = -36
    c: Radius(g0) = 2
FEATURE [PartDesign::Hole] Hole005  label="yCornerHole001"
  BaseFeature = -> Boolean003
  Depth = 25
  DepthType = 1
  Diameter = 4
  DrillForDepth = false
  DrillPoint = 1
  DrillPointAngle = 118
  HoleCutCountersinkAngle = 90
  HoleCutCustomValues = false
  HoleCutDepth = 0
  HoleCutDiameter = 4.1
  HoleCutType = 2
  ModelActualThread = false
  Profile = -> Sketch013
  Refine = true
  Tapered = false
  TaperedAngle = 90
  ThreadAngle = 0
  ThreadClass = 0
  ThreadCutOffInner = 0
  ThreadCutOffOuter = 0
  ThreadDirection = 0
  ThreadFit = 0
  ThreadPitch = 0
  ThreadSize = 0
  ThreadType = 0
  Threaded = false
FEATURE [Sketcher::SketchObject] Sketch014  label="zConerHoleSketch001"
  FullyConstrained = true
  MapMode = 5
  Placement = pos=(0,0,10) rot=(1,0,0;3.14159rad)
  Support = -> [Hole005]
  sketch-geometry (1):
    g0: Circle CenterX=-36 CenterY=-36 CenterZ=0 NormalX=0 NormalY=0 NormalZ=1 AngleXU=0 Radius=2
  constraints (3):
    c: DistanceX(g-1,g0) = -36
    c: DistanceY(g-1,g0) = -36
    c: Radius(g0) = 2
FEATURE [PartDesign::Hole] Hole006  label="zCornerHole001"
  BaseFeature = -> Hole005
  Depth = 25
  DepthType = 0
  Diameter = 4
  DrillForDepth = false
  DrillPoint = 1
  DrillPointAngle = 118
  HoleCutCountersinkAngle = 90
  HoleCutCustomValues = false
  HoleCutDepth = 0
  HoleCutDiameter = 6.1
  HoleCutType = 0
  ModelActualThread = false
  Profile = -> Sketch014
  Refine = true
  Tapered = false
  TaperedAngle = 90
  ThreadAngle = 0
  ThreadClass = 0
  ThreadCutOffInner = 0
  ThreadCutOffOuter = 0
  ThreadDirection = 0
  ThreadFit = 0
  ThreadPitch = 0
  ThreadSize = 0
  ThreadType = 0
  Threaded = false
FEATURE [Sketcher::SketchObject] Sketch015  label="xCornerHoleSketch001"
  FullyConstrained = true
  MapMode = 5
  Placement = pos=(-41,0,0) rot=(0.57735,0.57735,0.57735;2.0944rad)
  Support = -> [Hole006]
  sketch-geometry (1):
    g0: Circle CenterX=36 CenterY=5 CenterZ=0 NormalX=0 NormalY=0 NormalZ=1 AngleXU=0 Radius=2
  constraints (3):
    c: DistanceY(g0,g-1) = -5
    c: DistanceX(g-1,g0) = 36
    c: Radius(g0) = 2
FEATURE [PartDesign::Hole] Hole007  label="xCornerHole001"
  BaseFeature = -> Hole006
  Depth = 25
  DepthType = 0
  Diameter = 4
  DrillForDepth = false
  DrillPoint = 1
  DrillPointAngle = 118
  HoleCutCountersinkAngle = 90
  HoleCutCustomValues = false
  HoleCutDepth = 0
  HoleCutDiameter = 6.1
  HoleCutType = 0
  ModelActualThread = false
  Profile = -> Sketch015
  Refine = true
  Tapered = false
  TaperedAngle = 90
  ThreadAngle = 0
  ThreadClass = 0
  ThreadCutOffInner = 0
  ThreadCutOffOuter = 0
  ThreadDirection = 0
  ThreadFit = 0
  ThreadPitch = 0
  ThreadSize = 0
  ThreadType = 0
  Threaded = false
FEATURE [PartDesign::Body] Body006  label="TopCorner"
  Group = -> [Sketch012,Pad006,Boolean003,Sketch013,Hole005,Sketch014,Hole006,Sketch015,Hole007]
  Origin = -> Origin009
  Placement = pos=(0,0,78) rot=(0,1,0;0rad)
  Tip = -> Hole007
FEATURE [PartDesign::Boolean] Boolean002  label="boolWithPlateSupport"
  BaseFeature = -> Boolean
  Group = -> [Body002,Body006]
  Refine = true
  Type = 0
FEATURE [PartDesign::CoordinateSystem] LCS_Side
  AttacherType = Attacher::AttachEngine3D
  Support = -> [Boolean002]
FEATURE [App::Link] Bottom001  label="Bottom002"
  AttachedBy = #LCS_Plate
  AttachedTo = Parent Assembly#LCS_Origin
  AttachmentOffset = pos=(0,0,85) rot=(0,0,1;0rad)
  LinkPlacement = pos=(0,0,85) rot=(0,0,1;0rad)
  LinkedObject = -> Part
  Placement = pos=(0,0,85) rot=(0,0,1;0rad)
  SolverId = Placement::ExpressionEngine
  expr: Placement = LCS_Origin.Placement * AttachmentOffset * LCS_Plate.Placement ^ -1
FEATURE [App::Part] Assembly
  AssemblyType = Part::Link
  Group = -> [LCS_Origin,Variables,Constraints,Configurations,Bottom,Side,Side001,Side002,Side003,Bottom001]
  Origin = -> Origin007
  Type = Assembly
FEATURE [Sketcher::SketchObject] Sketch016
  FullyConstrained = true
  MapMode = 5
  Support = -> [XY_Plane012]
  sketch-geometry (5):
    g0: Circle CenterX=-36 CenterY=36 CenterZ=0 NormalX=0 NormalY=0 NormalZ=1 AngleXU=0 Radius=1.62
    g1: LineSegment StartX=-41 StartY=31 StartZ=0 EndX=-31 EndY=31 EndZ=0
    g2: LineSegment StartX=-31 StartY=31 StartZ=0 EndX=-31 EndY=41 EndZ=0
    g3: LineSegment StartX=-31 StartY=41 StartZ=0 EndX=-41 EndY=41 EndZ=0
    g4: LineSegment StartX=-41 StartY=41 StartZ=0 EndX=-41 EndY=31 EndZ=0
  constraints (14):
    c: Radius(g0) = 1.62
    c: Coincident(g1,g2)
    c: Coincident(g2,g3)
    c: Coincident(g3,g4)
    c: Coincident(g4,g1)
    c: Horizontal(g1)
    c: Horizontal(g3)
    c: Vertical(g2)
    c: Vertical(g4)
    c: Equal(g4,g1)
    c: Distance(g2) = 10
    c: Symmetric(g3,g1,g0)
    c: DistanceX(g0,g-1) = 36
    c: DistanceY(g-1,g0) = 36
FEATURE [PartDesign::Pad] Pad008
  Direction = (1,1,1)
  Length = 1.6
  Length2 = 100
  Profile = -> Sketch016
  Refine = true
  Type = 0
FEATURE [PartDesign::Body] Body009  label="BoardPositive"
  Group = -> [Sketch016,Pad008]
  Origin = -> Origin012
  Placement = pos=(0,0,-0.8) rot=(0,0,1;0rad)
  Tip = -> Pad008
FEATURE [Sketcher::SketchObject] Sketch017
  FullyConstrained = true
  MapMode = 5
  Support = -> [XY_Plane011]
  sketch-geometry (5):
    g0: Circle CenterX=-36 CenterY=36 CenterZ=0 NormalX=0 NormalY=0 NormalZ=1 AngleXU=0 Radius=1.62
    g1: LineSegment StartX=-43 StartY=31 StartZ=0 EndX=-31 EndY=31 EndZ=0
    g2: LineSegment StartX=-31 StartY=31 StartZ=0 EndX=-31 EndY=43 EndZ=0
    g3: LineSegment StartX=-31 StartY=43 StartZ=0 EndX=-43 EndY=43 EndZ=0
    g4: LineSegment StartX=-43 StartY=43 StartZ=0 EndX=-43 EndY=31 EndZ=0
  constraints (15):
    c: Radius(g0) = 1.62
    c: Coincident(g1,g2)
    c: Coincident(g2,g3)
    c: Coincident(g3,g4)
    c: Coincident(g4,g1)
    c: Horizontal(g1)
    c: Horizontal(g3)
    c: Vertical(g2)
    c: Vertical(g4)
    c: Equal(g4,g1)
    c: Distance(g2) = 12
    c: DistanceX(g0,g-1) = 36
    c: DistanceY(g-1,g0) = 36
    c: DistanceY(g1,g0) = 5
    c: DistanceX(g0,g1) = 5
FEATURE [PartDesign::Pad] Pad009
  Direction = (1,1,1)
  Length = 5.6
  Length2 = 100
  Midplane = true
  Profile = -> Sketch017
  Refine = true
  Type = 0
FEATURE [PartDesign::Boolean] Boolean004
  BaseFeature = -> Pad009
  Group = -> [Body009]
  Refine = true
  Type = 1
FEATURE [PartDesign::Body] Body008  label="BoardSupport"
  Group = -> [Sketch017,Pad009,Boolean004]
  Origin = -> Origin011
  Placement = pos=(0,0,76) rot=(0,0,1;0rad)
  Tip = -> Boolean004
FEATURE [Sketcher::SketchObject] Sketch018
  FullyConstrained = true
  MapMode = 5
  Support = -> [XY_Plane015]
  sketch-geometry (5):
    g0: Circle CenterX=-36 CenterY=36 CenterZ=0 NormalX=0 NormalY=0 NormalZ=1 AngleXU=0 Radius=1.62
    g1: LineSegment StartX=-41 StartY=31 StartZ=0 EndX=-31 EndY=31 EndZ=0
    g2: LineSegment StartX=-31 StartY=31 StartZ=0 EndX=-31 EndY=41 EndZ=0
    g3: LineSegment StartX=-31 StartY=41 StartZ=0 EndX=-41 EndY=41 EndZ=0
    g4: LineSegment StartX=-41 StartY=41 StartZ=0 EndX=-41 EndY=31 EndZ=0
  constraints (14):
    c: Radius(g0) = 1.62
    c: Coincident(g1,g2)
    c: Coincident(g2,g3)
    c: Coincident(g3,g4)
    c: Coincident(g4,g1)
    c: Horizontal(g1)
    c: Horizontal(g3)
    c: Vertical(g2)
    c: Vertical(g4)
    c: Equal(g4,g1)
    c: Distance(g2) = 10
    c: Symmetric(g3,g1,g0)
    c: DistanceX(g0,g-1) = 36
    c: DistanceY(g-1,g0) = 36
FEATURE [Sketcher::SketchObject] Sketch019
  FullyConstrained = true
  MapMode = 5
  Support = -> [XY_Plane014]
  sketch-geometry (5):
    g0: Circle CenterX=-36 CenterY=36 CenterZ=0 NormalX=0 NormalY=0 NormalZ=1 AngleXU=0 Radius=1.62
    g1: LineSegment StartX=-43 StartY=31 StartZ=0 EndX=-31 EndY=31 EndZ=0
    g2: LineSegment StartX=-31 StartY=31 StartZ=0 EndX=-31 EndY=43 EndZ=0
    g3: LineSegment StartX=-31 StartY=43 StartZ=0 EndX=-43 EndY=43 EndZ=0
    g4: LineSegment StartX=-43 StartY=43 StartZ=0 EndX=-43 EndY=31 EndZ=0
  constraints (15):
    c: Radius(g0) = 1.62
    c: Coincident(g1,g2)
    c: Coincident(g2,g3)
    c: Coincident(g3,g4)
    c: Coincident(g4,g1)
    c: Horizontal(g1)
    c: Horizontal(g3)
    c: Vertical(g2)
    c: Vertical(g4)
    c: Equal(g4,g1)
    c: Distance(g2) = 12
    c: DistanceX(g0,g-1) = 36
    c: DistanceY(g-1,g0) = 36
    c: DistanceY(g1,g0) = 5
    c: DistanceX(g0,g1) = 5
FEATURE [PartDesign::Pad] Pad010
  Direction = (1,1,1)
  Length = 1.6
  Length2 = 100
  Profile = -> Sketch018
  Refine = true
  Type = 0
FEATURE [PartDesign::Body] Body011  label="BoardPositive001"
  Group = -> [Sketch018,Pad010]
  Origin = -> Origin014
  Placement = pos=(0,0,-0.8) rot=(0,0,1;0rad)
  Tip = -> Pad010
FEATURE [PartDesign::Pad] Pad011
  Direction = (1,1,1)
  Length = 5.6
  Length2 = 100
  Midplane = true
  Profile = -> Sketch019
  Refine = true
  Type = 0
FEATURE [PartDesign::Boolean] Boolean005
  BaseFeature = -> Pad011
  Group = -> [Body011]
  Refine = true
  Type = 1
FEATURE [PartDesign::Body] Body010  label="BoardSupport001"
  Group = -> [Sketch019,Pad011,Boolean005]
  Origin = -> Origin013
  Placement = pos=(0,0,63) rot=(0,0,1;0rad)
  Tip = -> Boolean005
FEATURE [Sketcher::SketchObject] Sketch020
  FullyConstrained = true
  MapMode = 5
  Support = -> [XY_Plane017]
  sketch-geometry (5):
    g0: Circle CenterX=-36 CenterY=36 CenterZ=0 NormalX=0 NormalY=0 NormalZ=1 AngleXU=0 Radius=1.62
    g1: LineSegment StartX=-41 StartY=31 StartZ=0 EndX=-31 EndY=31 EndZ=0
    g2: LineSegment StartX=-31 StartY=31 StartZ=0 EndX=-31 EndY=41 EndZ=0
    g3: LineSegment StartX=-31 StartY=41 StartZ=0 EndX=-41 EndY=41 EndZ=0
    g4: LineSegment StartX=-41 StartY=41 StartZ=0 EndX=-41 EndY=31 EndZ=0
  constraints (14):
    c: Radius(g0) = 1.62
    c: Coincident(g1,g2)
    c: Coincident(g2,g3)
    c: Coincident(g3,g4)
    c: Coincident(g4,g1)
    c: Horizontal(g1)
    c: Horizontal(g3)
    c: Vertical(g2)
    c: Vertical(g4)
    c: Equal(g4,g1)
    c: Distance(g2) = 10
    c: Symmetric(g3,g1,g0)
    c: DistanceX(g0,g-1) = 36
    c: DistanceY(g-1,g0) = 36
FEATURE [Sketcher::SketchObject] Sketch021
  FullyConstrained = true
  MapMode = 5
  Support = -> [XY_Plane016]
  sketch-geometry (5):
    g0: Circle CenterX=-36 CenterY=36 CenterZ=0 NormalX=0 NormalY=0 NormalZ=1 AngleXU=0 Radius=1.62
    g1: LineSegment StartX=-43 StartY=31 StartZ=0 EndX=-31 EndY=31 EndZ=0
    g2: LineSegment StartX=-31 StartY=31 StartZ=0 EndX=-31 EndY=43 EndZ=0
    g3: LineSegment StartX=-31 StartY=43 StartZ=0 EndX=-43 EndY=43 EndZ=0
    g4: LineSegment StartX=-43 StartY=43 StartZ=0 EndX=-43 EndY=31 EndZ=0
  constraints (15):
    c: Radius(g0) = 1.62
    c: Coincident(g1,g2)
    c: Coincident(g2,g3)
    c: Coincident(g3,g4)
    c: Coincident(g4,g1)
    c: Horizontal(g1)
    c: Horizontal(g3)
    c: Vertical(g2)
    c: Vertical(g4)
    c: Equal(g4,g1)
    c: Distance(g2) = 12
    c: DistanceX(g0,g-1) = 36
    c: DistanceY(g-1,g0) = 36
    c: DistanceY(g1,g0) = 5
    c: DistanceX(g0,g1) = 5
FEATURE [PartDesign::Pad] Pad012
  Direction = (1,1,1)
  Length = 1.6
  Length2 = 100
  Profile = -> Sketch020
  Refine = true
  Type = 0
FEATURE [PartDesign::Body] Body013  label="BoardPositive002"
  Group = -> [Sketch020,Pad012]
  Origin = -> Origin016
  Placement = pos=(0,0,-0.8) rot=(0,0,1;0rad)
  Tip = -> Pad012
FEATURE [PartDesign::Pad] Pad013
  Direction = (1,1,1)
  Length = 5.6
  Length2 = 100
  Midplane = true
  Profile = -> Sketch021
  Refine = true
  Type = 0
FEATURE [PartDesign::Boolean] Boolean006
  BaseFeature = -> Pad013
  Group = -> [Body013]
  Refine = true
  Type = 1
FEATURE [PartDesign::Body] Body012  label="BoardSupport002"
  Group = -> [Sketch021,Pad013,Boolean006]
  Origin = -> Origin015
  Placement = pos=(0,0,50) rot=(0,0,1;0rad)
  Tip = -> Boolean006
FEATURE [Sketcher::SketchObject] Sketch022
  FullyConstrained = true
  MapMode = 5
  Support = -> [XY_Plane019]
  sketch-geometry (5):
    g0: Circle CenterX=-36 CenterY=36 CenterZ=0 NormalX=0 NormalY=0 NormalZ=1 AngleXU=0 Radius=1.62
    g1: LineSegment StartX=-41 StartY=31 StartZ=0 EndX=-31 EndY=31 EndZ=0
    g2: LineSegment StartX=-31 StartY=31 StartZ=0 EndX=-31 EndY=41 EndZ=0
    g3: LineSegment StartX=-31 StartY=41 StartZ=0 EndX=-41 EndY=41 EndZ=0
    g4: LineSegment StartX=-41 StartY=41 StartZ=0 EndX=-41 EndY=31 EndZ=0
  constraints (14):
    c: Radius(g0) = 1.62
    c: Coincident(g1,g2)
    c: Coincident(g2,g3)
    c: Coincident(g3,g4)
    c: Coincident(g4,g1)
    c: Horizontal(g1)
    c: Horizontal(g3)
    c: Vertical(g2)
    c: Vertical(g4)
    c: Equal(g4,g1)
    c: Distance(g2) = 10
    c: Symmetric(g3,g1,g0)
    c: DistanceX(g0,g-1) = 36
    c: DistanceY(g-1,g0) = 36
FEATURE [Sketcher::SketchObject] Sketch023
  FullyConstrained = true
  MapMode = 5
  Support = -> [XY_Plane018]
  sketch-geometry (5):
    g0: Circle CenterX=-36 CenterY=36 CenterZ=0 NormalX=0 NormalY=0 NormalZ=1 AngleXU=0 Radius=1.62
    g1: LineSegment StartX=-43 StartY=31 StartZ=0 EndX=-31 EndY=31 EndZ=0
    g2: LineSegment StartX=-31 StartY=31 StartZ=0 EndX=-31 EndY=43 EndZ=0
    g3: LineSegment StartX=-31 StartY=43 StartZ=0 EndX=-43 EndY=43 EndZ=0
    g4: LineSegment StartX=-43 StartY=43 StartZ=0 EndX=-43 EndY=31 EndZ=0
  constraints (15):
    c: Radius(g0) = 1.62
    c: Coincident(g1,g2)
    c: Coincident(g2,g3)
    c: Coincident(g3,g4)
    c: Coincident(g4,g1)
    c: Horizontal(g1)
    c: Horizontal(g3)
    c: Vertical(g2)
    c: Vertical(g4)
    c: Equal(g4,g1)
    c: Distance(g2) = 12
    c: DistanceX(g0,g-1) = 36
    c: DistanceY(g-1,g0) = 36
    c: DistanceY(g1,g0) = 5
    c: DistanceX(g0,g1) = 5
FEATURE [PartDesign::Pad] Pad014
  Direction = (1,1,1)
  Length = 1.6
  Length2 = 100
  Profile = -> Sketch022
  Refine = true
  Type = 0
FEATURE [PartDesign::Body] Body015  label="BoardPositive003"
  Group = -> [Sketch022,Pad014]
  Origin = -> Origin018
  Placement = pos=(0,0,-0.8) rot=(0,0,1;0rad)
  Tip = -> Pad014
FEATURE [PartDesign::Pad] Pad015
  Direction = (1,1,1)
  Length = 5.6
  Length2 = 100
  Midplane = true
  Profile = -> Sketch023
  Refine = true
  Type = 0
FEATURE [PartDesign::Boolean] Boolean007
  BaseFeature = -> Pad015
  Group = -> [Body015]
  Refine = true
  Type = 1
FEATURE [PartDesign::Body] Body014  label="BoardSupport003"
  Group = -> [Sketch023,Pad015,Boolean007]
  Origin = -> Origin017
  Placement = pos=(0,0,37) rot=(0,0,1;0rad)
  Tip = -> Boolean007
FEATURE [Sketcher::SketchObject] Sketch024
  FullyConstrained = true
  MapMode = 5
  Support = -> [XY_Plane021]
  sketch-geometry (5):
    g0: Circle CenterX=-36 CenterY=36 CenterZ=0 NormalX=0 NormalY=0 NormalZ=1 AngleXU=0 Radius=1.62
    g1: LineSegment StartX=-41 StartY=31 StartZ=0 EndX=-31 EndY=31 EndZ=0
    g2: LineSegment StartX=-31 StartY=31 StartZ=0 EndX=-31 EndY=41 EndZ=0
    g3: LineSegment StartX=-31 StartY=41 StartZ=0 EndX=-41 EndY=41 EndZ=0
    g4: LineSegment StartX=-41 StartY=41 StartZ=0 EndX=-41 EndY=31 EndZ=0
  constraints (14):
    c: Radius(g0) = 1.62
    c: Coincident(g1,g2)
    c: Coincident(g2,g3)
    c: Coincident(g3,g4)
    c: Coincident(g4,g1)
    c: Horizontal(g1)
    c: Horizontal(g3)
    c: Vertical(g2)
    c: Vertical(g4)
    c: Equal(g4,g1)
    c: Distance(g2) = 10
    c: Symmetric(g3,g1,g0)
    c: DistanceX(g0,g-1) = 36
    c: DistanceY(g-1,g0) = 36
FEATURE [Sketcher::SketchObject] Sketch025
  FullyConstrained = true
  MapMode = 5
  Support = -> [XY_Plane020]
  sketch-geometry (5):
    g0: Circle CenterX=-36 CenterY=36 CenterZ=0 NormalX=0 NormalY=0 NormalZ=1 AngleXU=0 Radius=1.62
    g1: LineSegment StartX=-43 StartY=31 StartZ=0 EndX=-31 EndY=31 EndZ=0
    g2: LineSegment StartX=-31 StartY=31 StartZ=0 EndX=-31 EndY=43 EndZ=0
    g3: LineSegment StartX=-31 StartY=43 StartZ=0 EndX=-43 EndY=43 EndZ=0
    g4: LineSegment StartX=-43 StartY=43 StartZ=0 EndX=-43 EndY=31 EndZ=0
  constraints (15):
    c: Radius(g0) = 1.62
    c: Coincident(g1,g2)
    c: Coincident(g2,g3)
    c: Coincident(g3,g4)
    c: Coincident(g4,g1)
    c: Horizontal(g1)
    c: Horizontal(g3)
    c: Vertical(g2)
    c: Vertical(g4)
    c: Equal(g4,g1)
    c: Distance(g2) = 12
    c: DistanceX(g0,g-1) = 36
    c: DistanceY(g-1,g0) = 36
    c: DistanceY(g1,g0) = 5
    c: DistanceX(g0,g1) = 5
FEATURE [PartDesign::Pad] Pad016
  Direction = (1,1,1)
  Length = 1.6
  Length2 = 100
  Profile = -> Sketch024
  Refine = true
  Type = 0
FEATURE [PartDesign::Body] Body017  label="BoardPositive004"
  Group = -> [Sketch024,Pad016]
  Origin = -> Origin020
  Placement = pos=(0,0,-0.8) rot=(0,0,1;0rad)
  Tip = -> Pad016
FEATURE [PartDesign::Pad] Pad017
  Direction = (1,1,1)
  Length = 5.6
  Length2 = 100
  Midplane = true
  Profile = -> Sketch025
  Refine = true
  Type = 0
FEATURE [PartDesign::Boolean] Boolean008
  BaseFeature = -> Pad017
  Group = -> [Body017]
  Refine = true
  Type = 1
FEATURE [PartDesign::Body] Body016  label="BoardSupport004"
  Group = -> [Sketch025,Pad017,Boolean008]
  Origin = -> Origin019
  Placement = pos=(0,0,24) rot=(0,0,1;0rad)
  Tip = -> Boolean008
FEATURE [PartDesign::Boolean] Boolean009  label="boolWithBoardSupport"
  BaseFeature = -> Boolean002
  Group = -> [Body008,Body010,Body012,Body014,Body016]
  Refine = true
  Type = 0
FEATURE [PartDesign::Body] Body001  label="Post"
  Group = -> [Sketch001,Pad001,Boolean,Boolean002,Boolean009]
  Origin = -> Origin003
  Tip = -> Boolean009
FEATURE [App::Part] Part001  label="Side"
  Group = -> [Body001,LCS_Side]
  Origin = -> Origin002
FEATURE [App::DocumentObjectGroup] Parts
  Group = -> [Part,Part001]
FEATURE [Fem::FemSolverObjectPython] SolverCcxTools  # FEM object (typed FeaturePython)
  AnalysisType = 3
  BeamShellResultOutput3D = false
  EigenmodeHighLimit = 1000000
  EigenmodeLowLimit = 0
  EigenmodesCount = 10
  GeometricalNonlinearity = 0
  IterationsControlParameterCutb = 0.25,0.5,0.75,0.85,,,1.5,
  IterationsControlParameterIter = 4,8,9,200,10,400,,200,,
  IterationsControlParameterTimeUse = false
  IterationsThermoMechMaximum = 2000
  IterationsUserDefinedIncrementations = false
  IterationsUserDefinedTimeStepLength = false
  MaterialNonlinearity = 0
  MatrixSolverType = 0
  SplitInputWriter = false
  ThermoMechSteadyState = true
  TimeEnd = 1
  TimeInitialStep = 0.01
FEATURE [Fem::FemMeshShapeNetgenObject] FEMMeshNetgen
  Fineness = 1
  GrowthRate = 0.3
  MaxSize = 1000
  NbSegsPerEdge = 1
  NbSegsPerRadius = 2
  Optimize = true
  SecondOrder = true
  Shape = -> Boolean009
FEATURE [Fem::ConstraintFixed] ConstraintFixed
  NormalDirection = (0,0,-1)
  Normals = (5) [(0,0,-1),(0,0,-1),(0,0,-1),(0,0,-1),(0,0,-1)]
  Points = (5) [(-45,40,0),(-40,45,0),(-45,45,0),(-50,45,0),(-45,50,0)]
  References = -> [Boolean009]
FEATURE [Fem::ConstraintForce] ConstraintForce
  DirectionVector = (0,1,0)
  Force = 10
  NormalDirection = (0,-1,0)
  Points = (12) [(-41,40,100),(-45,40,100),(-49,40,100),(-41,40,66.6667),(-45,40,66.6667),(-49,40,66.6667),(-41,40,33.3333),(-45,40,33.3333),(-49,40,33.3333),(-41,40,0),(-45,40,0),(-49,40,0)]
  References = -> [Boolean009]
  Reversed = true
FEATURE [App::MaterialObjectPython] MaterialSolid  # material (typed FeaturePython)
  Category = 0
  Material = AuthorAndLicense=CalculiX-Steel; CardName=CalculiX-Steel; Density=7900 kg/m^3; Description=Standard steel material for CalculiX sample calculations; Father=Metal; Name=CalculiX-Steel; PoissonRatio=0.3; SpecificHeat=590 J/kg/K; ThermalConductivity=43 W/m/K; ThermalExpansionCoefficient=0.000012 m/m/K; YoungsModulus=210000 MPa
FEATURE [Fem::FemAnalysis] Analysis
  Group = -> [SolverCcxTools,FEMMeshNetgen,ConstraintFixed,ConstraintForce,MaterialSolid]
